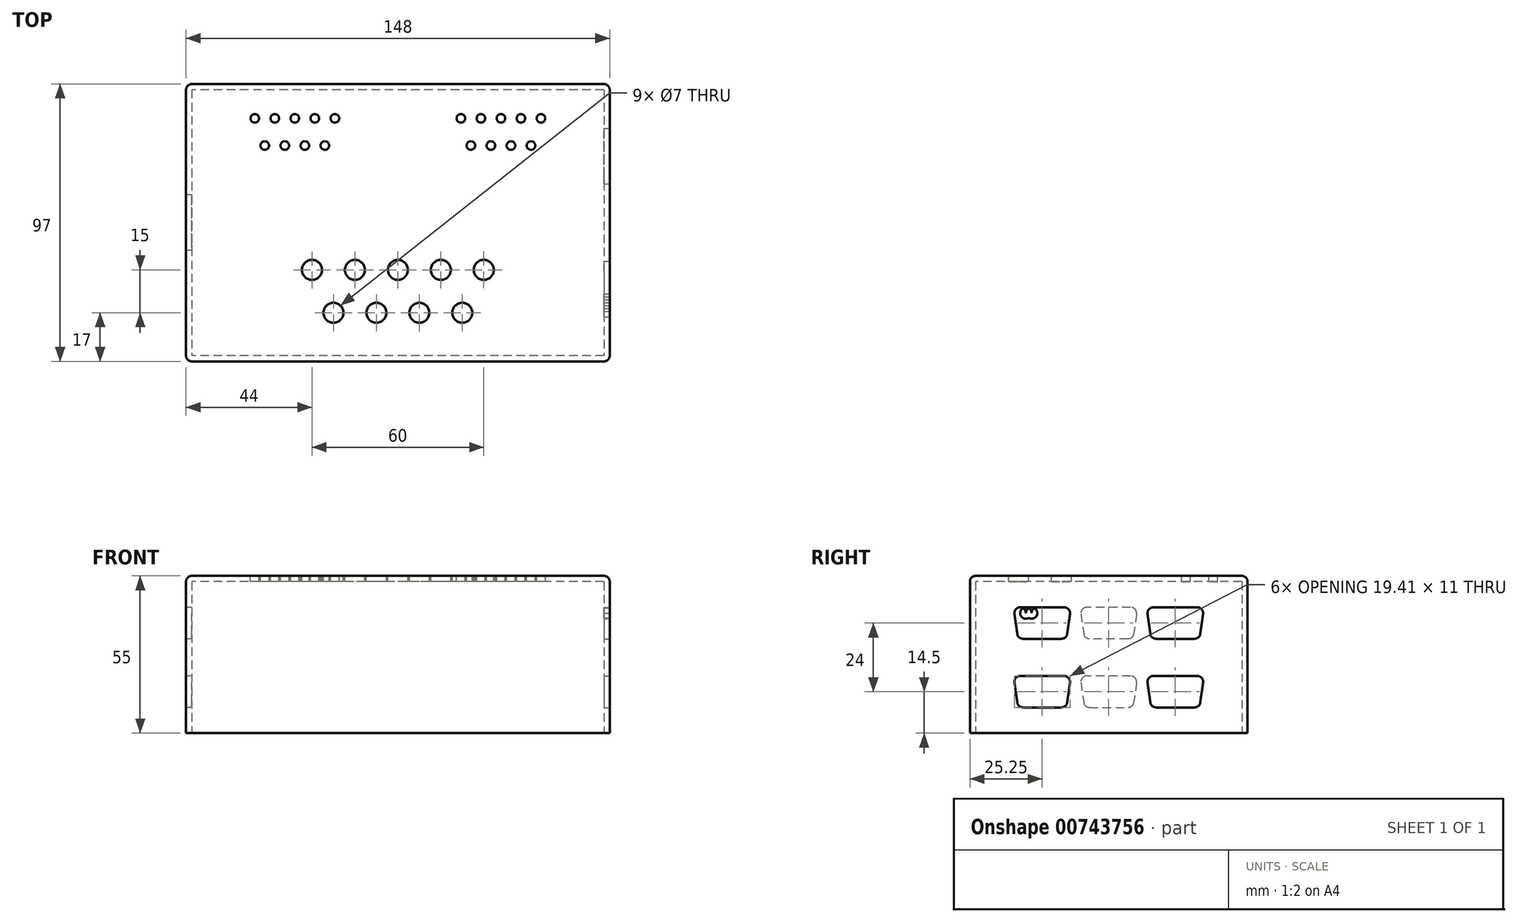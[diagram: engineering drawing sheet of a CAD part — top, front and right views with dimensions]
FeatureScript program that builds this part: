
annotation { "Feature Type Name" : "Feature", "Feature Type Description" : "" }
export const myFeature = defineFeature(function(context is Context, id is Id, definition is map)
    precondition{}
    {
        {
            var Q0;
            Q0=qCreatedBy(makeId("Top.planeOp"),FACE);
            var sketch = newSketch(context, id + "F0", { "sketchPlane" : qUnion([Q0])});
            skLineSegment(sketch, "E0.bottom", {"start": v(74, 48.5) * mm, "end": v(-74, 48.5) * mm});
            skLineSegment(sketch, "E0.top", {"start": v(74, -48.5) * mm, "end": v(-74, -48.5) * mm});
            skLineSegment(sketch, "E0.left", {"start": v(74, 48.5) * mm, "end": v(74, -48.5) * mm});
            skLineSegment(sketch, "E0.right", {"start": v(-74, 48.5) * mm, "end": v(-74, -48.5) * mm});
            skPoint(sketch, "E0.middle", {"position": v(0, 0) * mm});
            skSolve(sketch);
        }
        {
            var Q0;
            Q0=makeQuery(id+"F0.imprint","IMPRINT",FACE,{"disambiguationData":[TD([[makeQuery(id+"F0.imprint","IMPRINT",EDGE,{"derivedFrom":sQuery(id+"F0.wireOp",EDGE,"E0.bottom")}),1.0]])]});
            extrude(context, id + "F1", {"entities" : qUnion([Q0]), "depth" : 55 * mm, "offsetDistance" : 25 * mm});
        }
        {
            var Q0;
            Q0=makeQuery(id+"F1.opExtrude","CAP_FACE",FACE,{"disambiguationData":[OSD([sQuery(id+"F0.wireOp",EDGE,"E0.bottom"),sQuery(id+"F0.wireOp",EDGE,"E0.top"),sQuery(id+"F0.wireOp",EDGE,"E0.left"),sQuery(id+"F0.wireOp",EDGE,"E0.right")])],"isStart":true});
            shell(context, id + "F2", {"entities" : qUnion([Q0]), "thickness" : 2 * mm});
        }
        {
            var Q0;
            Q0=makeQuery(id+"F1.opExtrude","CAP_EDGE",EDGE,{"disambiguationData":[OSD([sQuery(id+"F0.wireOp",EDGE,"E0.top")])],"isStart":false});
            var Q1;
            Q1=makeQuery(id+"F1.opExtrude","CAP_EDGE",EDGE,{"disambiguationData":[OSD([sQuery(id+"F0.wireOp",EDGE,"E0.right")])],"isStart":false});
            var Q2;
            Q2=makeQuery(id+"F1.opExtrude","CAP_EDGE",EDGE,{"disambiguationData":[OSD([sQuery(id+"F0.wireOp",EDGE,"E0.left")])],"isStart":false});
            var Q3;
            Q3=makeQuery(id+"F1.opExtrude","CAP_EDGE",EDGE,{"disambiguationData":[OSD([sQuery(id+"F0.wireOp",EDGE,"E0.bottom")])],"isStart":false});
            var Q4;
            Q4=makeQuery(id+"F1.opExtrude","SWEPT_EDGE",EDGE,{"disambiguationData":[OSD([sQuery(id+"F0.wireOp",EDGE,"E0.top"),sQuery(id+"F0.wireOp",EDGE,"E0.right")])]});
            var Q5;
            Q5=makeQuery(id+"F1.opExtrude","SWEPT_EDGE",EDGE,{"disambiguationData":[OSD([sQuery(id+"F0.wireOp",EDGE,"E0.top"),sQuery(id+"F0.wireOp",EDGE,"E0.left")])]});
            var Q6;
            Q6=makeQuery(id+"F1.opExtrude","SWEPT_EDGE",EDGE,{"disambiguationData":[OSD([sQuery(id+"F0.wireOp",EDGE,"E0.bottom"),sQuery(id+"F0.wireOp",EDGE,"E0.left")])]});
            var Q7;
            Q7=makeQuery(id+"F1.opExtrude","SWEPT_EDGE",EDGE,{"disambiguationData":[OSD([sQuery(id+"F0.wireOp",EDGE,"E0.bottom"),sQuery(id+"F0.wireOp",EDGE,"E0.right")])]});
            fillet(context, id + "F3", {"entities" : qUnion([Q0, Q1, Q2, Q3, Q4, Q5, Q6, Q7]), "radius" : 2 * mm, "tangentPropagation" : true, "allowEdgeOverflow" : false});
        }
        {
            var Q0;
            Q0=makeQuery(id+"F1.opExtrude","CAP_FACE",FACE,{"disambiguationData":[OSD([sQuery(id+"F0.wireOp",EDGE,"E0.bottom"),sQuery(id+"F0.wireOp",EDGE,"E0.top"),sQuery(id+"F0.wireOp",EDGE,"E0.left"),sQuery(id+"F0.wireOp",EDGE,"E0.right")])],"isStart":false});
            var sketch = newSketch(context, id + "F4", { "sketchPlane" : qUnion([Q0])});
            skLineSegment(sketch, "E1", {"start": v(-72, 0) * mm, "end": v(72, 0) * mm, "construction": true});
            skLineSegment(sketch, "E2", {"start": v(0, 46.5) * mm, "end": v(0, -46.5) * mm, "construction": true});
            skCircle(sketch, "E3", {"center": v(-50, 36.5) * mm, "radius": 1.5 * mm});
            skCircle(sketch, "E4.1.0.0", {"center": v(-43, 36.5) * mm, "radius": 1.5 * mm});
            skCircle(sketch, "E4.2.0.0", {"center": v(-36, 36.5) * mm, "radius": 1.5 * mm});
            skCircle(sketch, "E4.3.0.0", {"center": v(-29, 36.5) * mm, "radius": 1.5 * mm});
            skCircle(sketch, "E4.4.0.0", {"center": v(-22, 36.5) * mm, "radius": 1.5 * mm});
            skLineSegment(sketch, "E4.direction1", {"start": v(-50, 36.5) * mm, "end": v(-43, 36.5) * mm, "construction": true});
            skCircle(sketch, "E5", {"center": v(-46.5, 27) * mm, "radius": 1.5 * mm});
            skCircle(sketch, "E6.1.0.0", {"center": v(-39.5, 27) * mm, "radius": 1.5 * mm});
            skCircle(sketch, "E6.2.0.0", {"center": v(-32.5, 27) * mm, "radius": 1.5 * mm});
            skCircle(sketch, "E6.3.0.0", {"center": v(-25.5, 27) * mm, "radius": 1.5 * mm});
            skLineSegment(sketch, "E6.direction1", {"start": v(-46.5, 27) * mm, "end": v(-39.5, 27) * mm, "construction": true});
            skCircle(sketch, "E7.MirrorC", {"center": v(50, 36.5) * mm, "radius": 1.5 * mm});
            skCircle(sketch, "E8.MirrorC", {"center": v(43, 36.5) * mm, "radius": 1.5 * mm});
            skCircle(sketch, "E9.MirrorC", {"center": v(36, 36.5) * mm, "radius": 1.5 * mm});
            skCircle(sketch, "E10.MirrorC", {"center": v(29, 36.5) * mm, "radius": 1.5 * mm});
            skCircle(sketch, "E11.MirrorC", {"center": v(22, 36.5) * mm, "radius": 1.5 * mm});
            skCircle(sketch, "E12.MirrorC", {"center": v(46.5, 27) * mm, "radius": 1.5 * mm});
            skCircle(sketch, "E13.MirrorC", {"center": v(39.5, 27) * mm, "radius": 1.5 * mm});
            skCircle(sketch, "E14.MirrorC", {"center": v(32.5, 27) * mm, "radius": 1.5 * mm});
            skCircle(sketch, "E15.MirrorC", {"center": v(25.5, 27) * mm, "radius": 1.5 * mm});
            skCircle(sketch, "E16", {"center": v(-30, -16.5) * mm, "radius": 3.5 * mm});
            skCircle(sketch, "E17.1.0.0", {"center": v(-15, -16.5) * mm, "radius": 3.5 * mm});
            skCircle(sketch, "E17.2.0.0", {"center": v(0, -16.5) * mm, "radius": 3.5 * mm});
            skCircle(sketch, "E17.3.0.0", {"center": v(15, -16.5) * mm, "radius": 3.5 * mm});
            skCircle(sketch, "E17.4.0.0", {"center": v(30, -16.5) * mm, "radius": 3.5 * mm});
            skLineSegment(sketch, "E17.direction1", {"start": v(-30, -16.5) * mm, "end": v(-15, -16.5) * mm, "construction": true});
            skCircle(sketch, "E18", {"center": v(-22.5, -31.5) * mm, "radius": 3.5 * mm});
            skPoint(sketch, "E18.centerSnap0", {"position": v(-22.5, -16.5) * mm});
            skCircle(sketch, "E19.1.0.0", {"center": v(-7.5, -31.5) * mm, "radius": 3.5 * mm});
            skCircle(sketch, "E19.2.0.0", {"center": v(7.5, -31.5) * mm, "radius": 3.5 * mm});
            skCircle(sketch, "E19.3.0.0", {"center": v(22.5, -31.5) * mm, "radius": 3.5 * mm});
            skLineSegment(sketch, "E19.direction1", {"start": v(-22.5, -31.5) * mm, "end": v(-7.5, -31.5) * mm, "construction": true});
            skSolve(sketch);
        }
        {
            var Q0;
            Q0 = qSketchRegion(id + "F4", true);
            extrude(context, id + "F5", {"entities" : qUnion([Q0]), "operationType" : NewBodyOperationType.REMOVE, "oppositeDirection" : true, "depth" : 3 * mm, "offsetDistance" : 25 * mm});
        }
        {
            var Q0;
            Q0=makeQuery(id+"F1.opExtrude","SWEPT_FACE",FACE,{"disambiguationData":[OSD([sQuery(id+"F0.wireOp",EDGE,"E0.right")])]});
            var sketch = newSketch(context, id + "F6", { "sketchPlane" : qUnion([Q0])});
            skLineSegment(sketch, "E20", {"start": v(0, 44) * mm, "end": v(-7.7, 44) * mm});
            skLineSegment(sketch, "E21", {"start": v(-9.7, 41.73) * mm, "end": v(-8.74, 34.73) * mm});
            skLineSegment(sketch, "E22", {"start": v(-6.75, 33) * mm, "end": v(0, 33) * mm});
            skLineSegment(sketch, "E23.MirrorCS", {"start": v(0, 44) * mm, "end": v(7.7, 44) * mm});
            skLineSegment(sketch, "E24.MirrorCS", {"start": v(9.7, 41.73) * mm, "end": v(8.74, 34.73) * mm});
            skLineSegment(sketch, "E25.MirrorCS", {"start": v(6.75, 33) * mm, "end": v(0, 33) * mm});
            skPoint(sketch, "E26.visualSharp", {"position": v(-10, 44) * mm});
            skArc(sketch, "E26.filletArc", {"start": v(-7.7, 44) * mm, "mid": v(-9.22, 43.32) * mm, "end": v(-9.7, 41.73) * mm});
            skPoint(sketch, "E27.visualSharp", {"position": v(-8.5, 33) * mm});
            skArc(sketch, "E27.filletArc", {"start": v(-8.74, 34.73) * mm, "mid": v(-8.07, 33.5) * mm, "end": v(-6.75, 33) * mm});
            skPoint(sketch, "E28.visualSharp", {"position": v(8.5, 33) * mm});
            skArc(sketch, "E28.filletArc", {"start": v(6.75, 33) * mm, "mid": v(8.07, 33.5) * mm, "end": v(8.74, 34.73) * mm});
            skPoint(sketch, "E29.visualSharp", {"position": v(10, 44) * mm});
            skArc(sketch, "E29.filletArc", {"start": v(9.7, 41.73) * mm, "mid": v(9.22, 43.32) * mm, "end": v(7.7, 44) * mm});
            skArc(sketch, "E30.0.1.0", {"start": v(9.7, 17.73) * mm, "mid": v(9.22, 19.32) * mm, "end": v(7.7, 20) * mm});
            skPoint(sketch, "E30.0.1.1", {"position": v(-8.5, 9) * mm});
            skLineSegment(sketch, "E30.0.1.2", {"start": v(0, 20) * mm, "end": v(-7.7, 20) * mm});
            skPoint(sketch, "E30.0.1.3", {"position": v(10, 20) * mm});
            skPoint(sketch, "E30.0.1.4", {"position": v(8.5, 9) * mm});
            skLineSegment(sketch, "E30.0.1.5", {"start": v(-6.75, 9) * mm, "end": v(0, 9) * mm});
            skLineSegment(sketch, "E30.0.1.6", {"start": v(0, 20) * mm, "end": v(7.7, 20) * mm});
            skLineSegment(sketch, "E30.0.1.7", {"start": v(6.75, 9) * mm, "end": v(0, 9) * mm});
            skLineSegment(sketch, "E30.0.1.8", {"start": v(9.7, 17.73) * mm, "end": v(8.74, 10.73) * mm});
            skLineSegment(sketch, "E30.0.1.9", {"start": v(-9.7, 17.73) * mm, "end": v(-8.74, 10.73) * mm});
            skPoint(sketch, "E30.0.1.10", {"position": v(-10, 20) * mm});
            skArc(sketch, "E30.0.1.11", {"start": v(6.75, 9) * mm, "mid": v(8.07, 9.5) * mm, "end": v(8.74, 10.73) * mm});
            skArc(sketch, "E30.0.1.12", {"start": v(-8.74, 10.73) * mm, "mid": v(-8.07, 9.5) * mm, "end": v(-6.75, 9) * mm});
            skArc(sketch, "E30.0.1.13", {"start": v(-7.7, 20) * mm, "mid": v(-9.22, 19.32) * mm, "end": v(-9.7, 17.73) * mm});
            skLineSegment(sketch, "E30.direction1", {"start": v(-8.5, 33) * mm, "end": v(17, 33) * mm, "construction": true});
            skLineSegment(sketch, "E30.direction2", {"start": v(-8.5, 33) * mm, "end": v(-8.5, 9) * mm, "construction": true});
            skSolve(sketch);
        }
        {
            var Q0;
            Q0 = qSketchRegion(id + "F6", true);
            extrude(context, id + "F7", {"entities" : qUnion([Q0]), "operationType" : NewBodyOperationType.REMOVE, "oppositeDirection" : true, "depth" : 3 * mm, "offsetDistance" : 25 * mm});
        }
        {
            var Q0;
            Q0=makeQuery(id+"F1.opExtrude","SWEPT_FACE",FACE,{"disambiguationData":[OSD([sQuery(id+"F0.wireOp",EDGE,"E0.left")])]});
            var sketch = newSketch(context, id + "F8", { "sketchPlane" : qUnion([Q0])});
            skLineSegment(sketch, "E31", {"start": v(-23.25, 46.9) * mm, "end": v(-23.25, 11.29) * mm, "construction": true});
            skLineSegment(sketch, "E32", {"start": v(-23.25, 44) * mm, "end": v(-30.96, 44) * mm});
            skLineSegment(sketch, "E33", {"start": v(-32.94, 41.73) * mm, "end": v(-31.99, 34.73) * mm});
            skLineSegment(sketch, "E34", {"start": v(-30, 33) * mm, "end": v(-23.25, 33) * mm});
            skPoint(sketch, "E35.visualSharp", {"position": v(-33.25, 44) * mm});
            skArc(sketch, "E35.filletArc", {"start": v(-30.96, 44) * mm, "mid": v(-32.47, 43.32) * mm, "end": v(-32.94, 41.73) * mm});
            skPoint(sketch, "E36.visualSharp", {"position": v(-31.75, 33) * mm});
            skArc(sketch, "E36.filletArc", {"start": v(-31.99, 34.73) * mm, "mid": v(-31.32, 33.5) * mm, "end": v(-30, 33) * mm});
            skLineSegment(sketch, "E37", {"start": v(0, 53) * mm, "end": v(0, 0) * mm, "construction": true});
            skArc(sketch, "E38.MirrorCS", {"start": v(-14.51, 34.73) * mm, "mid": v(-15.18, 33.5) * mm, "end": v(-16.5, 33) * mm});
            skArc(sketch, "E39.MirrorCS", {"start": v(-15.54, 44) * mm, "mid": v(-14.03, 43.32) * mm, "end": v(-13.56, 41.73) * mm});
            skLineSegment(sketch, "E40.MirrorCS", {"start": v(-16.5, 33) * mm, "end": v(-23.25, 33) * mm});
            skLineSegment(sketch, "E41.MirrorCS", {"start": v(-13.56, 41.73) * mm, "end": v(-14.51, 34.73) * mm});
            skPoint(sketch, "E42.MirrorP", {"position": v(-13.25, 44) * mm});
            skPoint(sketch, "E43.MirrorP", {"position": v(-14.75, 33) * mm});
            skLineSegment(sketch, "E44.MirrorCS", {"start": v(-23.25, 44) * mm, "end": v(-15.54, 44) * mm});
            skLineSegment(sketch, "E45.0.1.0", {"start": v(-30, 9) * mm, "end": v(-23.25, 9) * mm});
            skLineSegment(sketch, "E45.0.1.1", {"start": v(-32.94, 17.73) * mm, "end": v(-31.99, 10.73) * mm});
            skPoint(sketch, "E45.0.1.2", {"position": v(-33.25, 20) * mm});
            skPoint(sketch, "E45.0.1.3", {"position": v(-31.75, 9) * mm});
            skLineSegment(sketch, "E45.0.1.4", {"start": v(-23.25, 20) * mm, "end": v(-30.96, 20) * mm});
            skLineSegment(sketch, "E45.0.1.5", {"start": v(-16.5, 9) * mm, "end": v(-23.25, 9) * mm});
            skLineSegment(sketch, "E45.0.1.6", {"start": v(-13.56, 17.73) * mm, "end": v(-14.51, 10.73) * mm});
            skLineSegment(sketch, "E45.0.1.7", {"start": v(-23.25, 20) * mm, "end": v(-15.54, 20) * mm});
            skPoint(sketch, "E45.0.1.8", {"position": v(-14.75, 9) * mm});
            skPoint(sketch, "E45.0.1.9", {"position": v(-13.25, 20) * mm});
            skArc(sketch, "E45.0.1.10", {"start": v(-31.99, 10.73) * mm, "mid": v(-31.32, 9.5) * mm, "end": v(-30, 9) * mm});
            skArc(sketch, "E45.0.1.11", {"start": v(-30.96, 20) * mm, "mid": v(-32.47, 19.32) * mm, "end": v(-32.94, 17.73) * mm});
            skArc(sketch, "E45.0.1.12", {"start": v(-14.51, 10.73) * mm, "mid": v(-15.18, 9.5) * mm, "end": v(-16.5, 9) * mm});
            skArc(sketch, "E45.0.1.13", {"start": v(-15.54, 20) * mm, "mid": v(-14.03, 19.32) * mm, "end": v(-13.56, 17.73) * mm});
            skLineSegment(sketch, "E45.1.0.0", {"start": v(16.5, 33) * mm, "end": v(23.25, 33) * mm});
            skLineSegment(sketch, "E45.1.0.1", {"start": v(13.56, 41.73) * mm, "end": v(14.51, 34.73) * mm});
            skPoint(sketch, "E45.1.0.2", {"position": v(13.25, 44) * mm});
            skPoint(sketch, "E45.1.0.3", {"position": v(14.75, 33) * mm});
            skLineSegment(sketch, "E45.1.0.4", {"start": v(23.25, 44) * mm, "end": v(15.54, 44) * mm});
            skLineSegment(sketch, "E45.1.0.5", {"start": v(30, 33) * mm, "end": v(23.25, 33) * mm});
            skLineSegment(sketch, "E45.1.0.6", {"start": v(32.94, 41.73) * mm, "end": v(31.99, 34.73) * mm});
            skLineSegment(sketch, "E45.1.0.7", {"start": v(23.25, 44) * mm, "end": v(30.96, 44) * mm});
            skPoint(sketch, "E45.1.0.8", {"position": v(31.75, 33) * mm});
            skPoint(sketch, "E45.1.0.9", {"position": v(33.25, 44) * mm});
            skArc(sketch, "E45.1.0.10", {"start": v(14.51, 34.73) * mm, "mid": v(15.18, 33.5) * mm, "end": v(16.5, 33) * mm});
            skArc(sketch, "E45.1.0.11", {"start": v(15.54, 44) * mm, "mid": v(14.03, 43.32) * mm, "end": v(13.56, 41.73) * mm});
            skArc(sketch, "E45.1.0.12", {"start": v(31.99, 34.73) * mm, "mid": v(31.32, 33.5) * mm, "end": v(30, 33) * mm});
            skArc(sketch, "E45.1.0.13", {"start": v(30.96, 44) * mm, "mid": v(32.47, 43.32) * mm, "end": v(32.94, 41.73) * mm});
            skLineSegment(sketch, "E45.1.1.0", {"start": v(16.5, 9) * mm, "end": v(23.25, 9) * mm});
            skLineSegment(sketch, "E45.1.1.1", {"start": v(13.56, 17.73) * mm, "end": v(14.51, 10.73) * mm});
            skPoint(sketch, "E45.1.1.2", {"position": v(13.25, 20) * mm});
            skPoint(sketch, "E45.1.1.3", {"position": v(14.75, 9) * mm});
            skLineSegment(sketch, "E45.1.1.4", {"start": v(23.25, 20) * mm, "end": v(15.54, 20) * mm});
            skLineSegment(sketch, "E45.1.1.5", {"start": v(30, 9) * mm, "end": v(23.25, 9) * mm});
            skLineSegment(sketch, "E45.1.1.6", {"start": v(32.94, 17.73) * mm, "end": v(31.99, 10.73) * mm});
            skLineSegment(sketch, "E45.1.1.7", {"start": v(23.25, 20) * mm, "end": v(30.96, 20) * mm});
            skPoint(sketch, "E45.1.1.8", {"position": v(31.75, 9) * mm});
            skPoint(sketch, "E45.1.1.9", {"position": v(33.25, 20) * mm});
            skArc(sketch, "E45.1.1.10", {"start": v(14.51, 10.73) * mm, "mid": v(15.18, 9.5) * mm, "end": v(16.5, 9) * mm});
            skArc(sketch, "E45.1.1.11", {"start": v(15.54, 20) * mm, "mid": v(14.03, 19.32) * mm, "end": v(13.56, 17.73) * mm});
            skArc(sketch, "E45.1.1.12", {"start": v(31.99, 10.73) * mm, "mid": v(31.32, 9.5) * mm, "end": v(30, 9) * mm});
            skArc(sketch, "E45.1.1.13", {"start": v(30.96, 20) * mm, "mid": v(32.47, 19.32) * mm, "end": v(32.94, 17.73) * mm});
            skLineSegment(sketch, "E45.direction1", {"start": v(-31.75, 33) * mm, "end": v(14.75, 33) * mm, "construction": true});
            skLineSegment(sketch, "E45.direction2", {"start": v(-31.75, 33) * mm, "end": v(-31.75, 9) * mm, "construction": true});
            skCircle(sketch, "E46", {"center": v(-30.96, 42) * mm, "radius": 2 * mm});
            skCircle(sketch, "E47", {"center": v(-30, 35) * mm, "radius": 2 * mm});
            skCircle(sketch, "E48", {"center": v(-16.5, 35) * mm, "radius": 2 * mm});
            skCircle(sketch, "E49", {"center": v(-15.54, 42) * mm, "radius": 2 * mm});
            skCircle(sketch, "E50", {"center": v(-28.96, 42) * mm, "radius": 2 * mm});
            skCircle(sketch, "E51", {"center": v(-26.96, 42) * mm, "radius": 2 * mm});
            skCircle(sketch, "E52", {"center": v(-24.96, 42) * mm, "radius": 2 * mm});
            skSolve(sketch);
        }
        {
            var Q0;
            Q0 = qSketchRegion(id + "F8", true);
            extrude(context, id + "F9", {"entities" : qUnion([Q0]), "operationType" : NewBodyOperationType.REMOVE, "oppositeDirection" : true, "depth" : 3 * mm, "offsetDistance" : 25 * mm});
        }
    });
